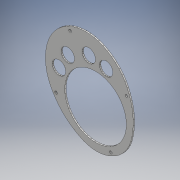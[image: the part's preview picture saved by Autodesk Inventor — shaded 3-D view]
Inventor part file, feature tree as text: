
AUTODESK INVENTOR PART (.ipt)
format: ipt  version: 2018 (Build 220112000, 112)  size: 409,088 bytes
history: native  units: mm
features: extrude x1, sketch x1
ambient origin geometry x8: Origin, YZ Plane, XZ Plane, XY Plane, X Axis, Y Axis, Z Axis, Center Point
bodies: Solid1 (feature_tree)
feature tree (2):
  extrude  "Extrusion1"  [1 undecoded]
  sketch  "Sketch1"  dims[d0=1.0mm d1=0.0mm]
note: 1 required parameter value undecoded (feature->parameter linkage not recoverable at this tier; creation-order binding heuristic only, values carry confidence <= 0.55)
